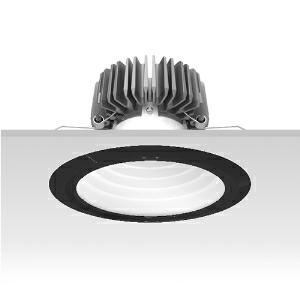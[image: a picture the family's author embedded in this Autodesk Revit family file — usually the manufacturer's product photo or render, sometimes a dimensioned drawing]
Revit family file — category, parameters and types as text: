
# Revit family: 3f_filippi_-_3f_reno_bianco_ampio_3f_filippi_-_30646_a01026_-_3f_reno_200_wh_2000-840_ep_wide___vt_bk_7ca8
name_source: partatom
category: Lighting Fixtures
units: mm (PartAtom-declared; Revit-internal decimal feet)

## family parameters
Cut with Voids When Loaded = No
Host = Face
Light Source = No
Part Type = Normal
Room Calculation Point = No
Round Connector Dimension = Use Diameter
Shared = No

## types (1)
- 3F Filippi - 3F Reno Bianco Ampio (1 x LED, 1884 lm, 21 W, 4000 K)
    Apparent Load = 21 VA
    Approval mark = ENEC
    CIE Flux Codes = 75 94 99 100 100
    Color Rendering = 80
    Color Temperature = 4000 K
    Control Gear = Electronic ballast
    Default Elevation = 1800 mm
    Description = ILLUMINOTECHNICAL
Luminous efficiency 100% (DLOR 100%, ULOR 0%).
Initial luminous flux of the luminaire 1884 lm.
Emergency luminaire luminous flux BLF 20%.
Direct symmetric wide distribution.
Installation Interdistance Transv.D = 1.56 x hu - Long.D = 1.56 x hu.
Average luminance <3000 cd/m² for radial angles >65°.
Tabular UGR (CIE 117 - 4H-8H; S=0.25H; 70/50/20): RUG 20.8 - 20.6.
Beam angle: 74° - 74°.
Luminous efficacy 90 lm/W.
Lifetime (L90/B10): 30000 h. (tq+25°C)
Lifetime (L85/B10): 50000 h. (tq+25°C)
Lifetime (L70/B10): 80000 h. (tq+25°C)
Sudden decreased luminous flux after 50000 hours: 0% (C0).
Photobiological safety in compliance with IEC/TR 62778: RG0 risk exempt, (IEC 62471).
In compliance with IEC/EN 62722-2-1 - IEC/EN 62717 standards.

SOURCE
Compact LED module 2000/840.
Energy efficiency class (UE 2019/2020 - UE 2019/2015): D.
CIE 13.3 Colour rendering index: CRI >80 (R9 <50%).
IES TM-30 Fidelity Index: Rf = 84 Rg = 95.
CCT nominal colour temperature 4000 K.
Colour initial tolerance (MacAdam): SDCM 3.
Zhaga Book 3 compliant.

MECHANICAL
Passive heat dissipator in die-casting aluminium, oversized, for optimum thermal management of the LED module.
Parabolic element with graduated/concentric rings in white polycarbonate.
Transparent external lens with glossy and satin differentiated surfaces, with a cooling and anti-insect system in methacrylate (PMMA).
Fastening spring clips in stainless steel.
Dimensions: diameter 226 mm, height 146 mm. Weight 1.535 kg.
IP44 protection degree for exposed part, IP20 for recessed part.
Mechanical strength to impacts IK06 (1 joule).
Glow-wire test resistance 650°C.

ELECTRICAL
Wiring on a separate unit.
Halogen Free electronic wiring 230V-50/60Hz, power factor 0.90, THD <25%, constant output current, SELV, class II, 1 driver.
Power of the luminaire 21 W.
CE - IEC 60598-1 - EN 60598-1.
EP maintained emergency wiring on board, 1h duration, 24h recharge; compliant with EN 60598-2-22, excluding high risk areas.
SAFE FLICKER: PstLM=<1 and SVM=<0.4 (IEC TR 61547-1 and IEC TR 63158), to ensure a more comfortable and safe light.
Ambient temperature from +5°C to +25°C.
Temperature class T6 max 85°C.
Relative humidity UR: <85%.

INSTALLATION
Pull-up recessed fitting.
False ceiling carving: 200 mm.
All accessories dedicated to this product are available on the Catalog and on our website www.3F-Filippi.com.

ACCESSORIES
A01026 - VT transparent glass, tempered, not flammable, locked and in line with the trim, in black polycarbonate.

APPLICATIONS
Environments: architectural, commercial, exhibition areas, transit areas, corridors, shops, display windows, service areas.
In false ceilings with narrow voids.

WARNING
Luminaire designed for disposal/recycling at end-of-life.
Replaceable (LED only) light source by a professional. Replaceable control gear by a professional.
    Height = 0 mm  [stored 0 ft]
    Lamp = 1 x LED
    Lamp Light Flux = 1884 lm
    Lamp Power = 21 W
    Lamp count = 1
    Length = 226 mm
    Lifetime = 50000 h
    Luminous efficacy = 90 lm/W
    Manufacturer = 3F Filippi
    ModVariant = No
    Model = 3F Filippi - 30646+A01026 - 3F Reno 200 WH 2000-840 EP WIDE + VT BK
    Mounting Place = Ceiling
    Mounting Type = Recessed
    Number of Poles = 1
    OnlyDefault = Yes
    Power Factor = 1
    Product Name = 3F Filippi - 3F Reno Bianco Ampio
    Product group = recessed luminaire
    ProductGroupID = 4
    Protection Class = Protection class II
    Protection Degree = IP 20
    RLX_Detail_Level = 1
    RLX_Emergency_Light_Flux = 0 lm
    RLX_Emergency_Type = 0
    RLX_Emergency_Type_DB = No
    RlxData = <blob elided: 100053 chars, md5=7860bb52>
    Socket = socket
    Standby Power = 0 W
    System Light Flux = 1884 lm
    System Power = 21 W
    Type Comments = Product without accessories
    Type Image = 3ffilippi_3f_reno_200_wh__a01026.jpg
    URL = http://relux.com
    VarID = ---
    Voltage = 0 V
    Weight = 0.00 kg
    Width = 0 mm  [stored 0 ft]

note: [stored X ft] marks values corroborated as IEEE doubles in the binary element streams (Revit-internal decimal feet)

## geometry (parser evidence)
native form markers: Blend x4, Sweep x11
no freeform markers — native parametric forms only
